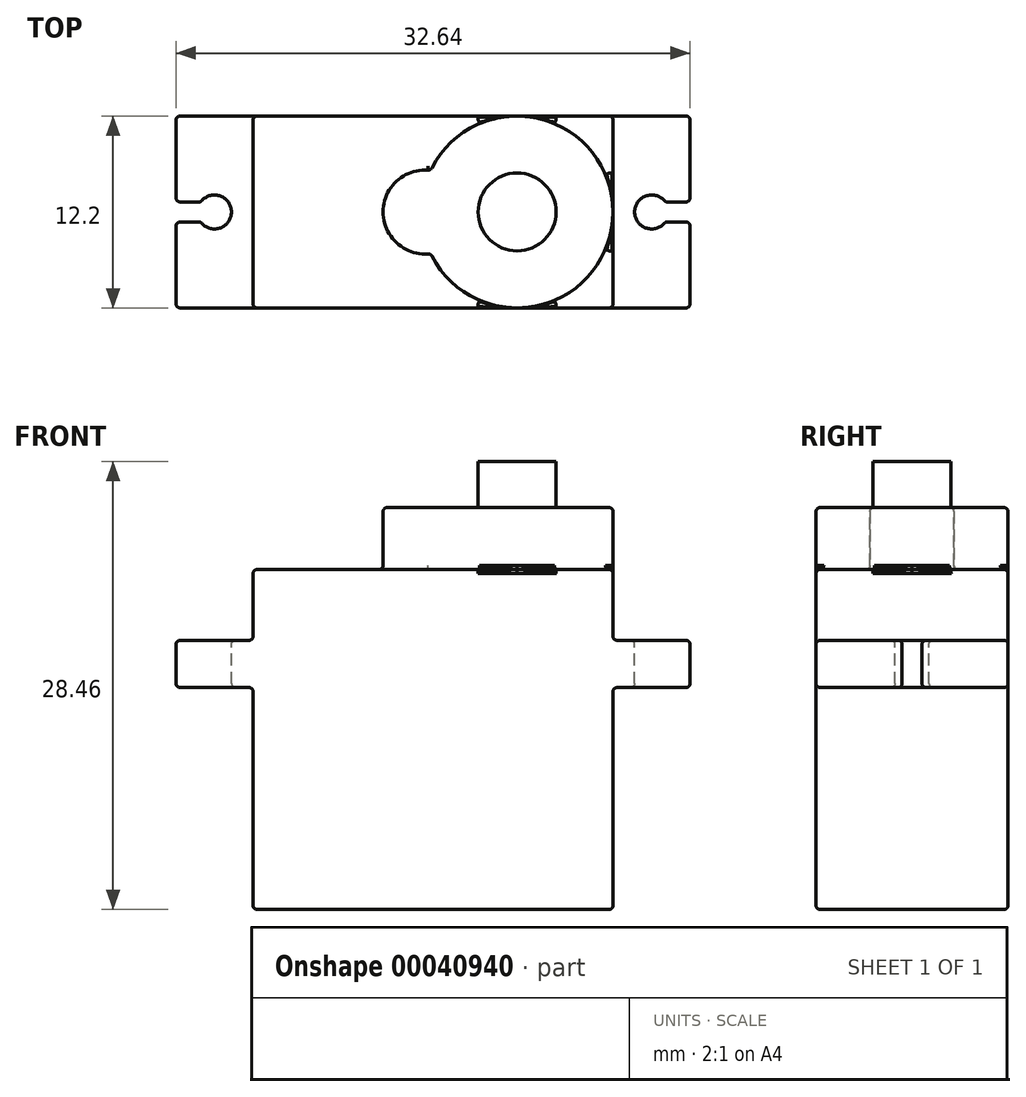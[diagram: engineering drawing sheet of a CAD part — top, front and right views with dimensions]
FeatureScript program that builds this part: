
annotation { "Feature Type Name" : "Feature", "Feature Type Description" : "" }
export const myFeature = defineFeature(function(context is Context, id is Id, definition is map)
    precondition{}
    {
        {
            var Q0;
            Q0=qCreatedBy(makeId("Top.planeOp"),FACE);
            var sketch = newSketch(context, id + "F0", { "sketchPlane" : qUnion([Q0])});
            skLineSegment(sketch, "E0.rect.bottom", {"start": v(11.43, 6.1) * mm, "end": v(-11.43, 6.1) * mm});
            skLineSegment(sketch, "E0.rect.top", {"start": v(11.43, -6.1) * mm, "end": v(-11.43, -6.1) * mm});
            skLineSegment(sketch, "E0.rect.left", {"start": v(11.43, 6.1) * mm, "end": v(11.43, -6.1) * mm});
            skLineSegment(sketch, "E0.rect.right", {"start": v(-11.43, 6.1) * mm, "end": v(-11.43, -6.1) * mm});
            skPoint(sketch, "E0.rect.middle", {"position": v(0, 0) * mm});
            skSolve(sketch);
        }
        {
            var Q0;
            Q0=makeQuery(id+"F0.imprint","IMPRINT",FACE,{"disambiguationData":[TD([[makeQuery(id+"F0.imprint","IMPRINT",EDGE,{"derivedFrom":sQuery(id+"F0.wireOp",EDGE,"E0.rect.bottom")}),1.0]])]});
            extrude(context, id + "F1", {"entities" : qUnion([Q0]), "depth" : 4.5 * mm});
        }
        {
            var Q0;
            Q0=qCreatedBy(makeId("Top.planeOp"),FACE);
            var sketch = newSketch(context, id + "F2", { "sketchPlane" : qUnion([Q0])});
            skLineSegment(sketch, "E1.rect.bottom", {"start": v(-16.32, 6.1) * mm, "end": v(16.32, 6.1) * mm});
            skLineSegment(sketch, "E1.rect.top", {"start": v(-16.32, -6.1) * mm, "end": v(16.32, -6.1) * mm});
            skLineSegment(sketch, "E1.rect.left", {"start": v(-16.32, 6.1) * mm, "end": v(-16.32, 0.64) * mm});
            skLineSegment(sketch, "E1.rect.right", {"start": v(16.32, 6.1) * mm, "end": v(16.32, 0.64) * mm});
            skPoint(sketch, "E1.rect.middle", {"position": v(0, 0) * mm});
            skArc(sketch, "E2", {"start": v(-14.75, -0.64) * mm, "mid": v(-12.8, 0) * mm, "end": v(-14.75, 0.64) * mm});
            skArc(sketch, "E3", {"start": v(14.75, 0.64) * mm, "mid": v(12.8, 0) * mm, "end": v(14.75, -0.64) * mm});
            skLineSegment(sketch, "E4.rect.bottom", {"start": v(-16.32, 0.64) * mm, "end": v(-14.75, 0.64) * mm});
            skLineSegment(sketch, "E4.rect.top", {"start": v(-16.32, -0.64) * mm, "end": v(-14.75, -0.64) * mm});
            skLineSegment(sketch, "E5.rect.bottom", {"start": v(16.32, 0.64) * mm, "end": v(14.75, 0.64) * mm});
            skLineSegment(sketch, "E5.rect.top", {"start": v(16.32, -0.64) * mm, "end": v(14.75, -0.64) * mm});
            skLineSegment(sketch, "E6.trimOffspring", {"start": v(16.32, -0.64) * mm, "end": v(16.32, -6.1) * mm});
            skLineSegment(sketch, "E7.trimOffspring", {"start": v(-16.32, -0.63) * mm, "end": v(-16.32, -6.1) * mm});
            skSolve(sketch);
        }
        {
            var Q0;
            Q0=makeQuery(id+"F2.imprint","IMPRINT",FACE,{"disambiguationData":[TD([[makeQuery(id+"F2.imprint","IMPRINT",EDGE,{"derivedFrom":sQuery(id+"F2.wireOp",EDGE,"E1.rect.bottom")}),-1.0]])]});
            extrude(context, id + "F3", {"entities" : qUnion([Q0]), "operationType" : NewBodyOperationType.ADD, "oppositeDirection" : true, "depth" : 3 * mm});
        }
        {
            var Q0;
            Q0=makeQuery(id+"F3.opExtrude","CAP_FACE",FACE,{"disambiguationData":[OSD([sQuery(id+"F2.wireOp",EDGE,"E1.rect.bottom"),sQuery(id+"F2.wireOp",EDGE,"E1.rect.top"),sQuery(id+"F2.wireOp",EDGE,"E1.rect.left"),sQuery(id+"F2.wireOp",EDGE,"E1.rect.right"),sQuery(id+"F2.wireOp",EDGE,"E2"),sQuery(id+"F2.wireOp",EDGE,"E3"),sQuery(id+"F2.wireOp",EDGE,"E4.rect.bottom"),sQuery(id+"F2.wireOp",EDGE,"E4.rect.top"),sQuery(id+"F2.wireOp",EDGE,"E5.rect.bottom"),sQuery(id+"F2.wireOp",EDGE,"E5.rect.top"),sQuery(id+"F2.wireOp",EDGE,"E6.trimOffspring"),sQuery(id+"F2.wireOp",EDGE,"E7.trimOffspring")])],"isStart":false});
            var sketch = newSketch(context, id + "F4", { "sketchPlane" : qUnion([Q0])});
            skLineSegment(sketch, "E8.rect.bottom", {"start": v(11.43, 6.1) * mm, "end": v(-11.43, 6.1) * mm});
            skLineSegment(sketch, "E8.rect.top", {"start": v(11.43, -6.1) * mm, "end": v(-11.43, -6.1) * mm});
            skLineSegment(sketch, "E8.rect.left", {"start": v(11.43, 6.1) * mm, "end": v(11.43, -6.1) * mm});
            skLineSegment(sketch, "E8.rect.right", {"start": v(-11.43, 6.1) * mm, "end": v(-11.43, -6.1) * mm});
            skPoint(sketch, "E8.rect.middle", {"position": v(0, 0) * mm});
            skSolve(sketch);
        }
        {
            var Q0;
            Q0=makeQuery(id+"F4.imprint","IMPRINT",FACE,{"disambiguationData":[TD([[makeQuery(id+"F4.imprint","IMPRINT",EDGE,{"derivedFrom":sQuery(id+"F4.wireOp",EDGE,"E8.rect.bottom")}),-1.0]])]});
            extrude(context, id + "F5", {"entities" : qUnion([Q0]), "operationType" : NewBodyOperationType.ADD, "depth" : 14.1 * mm});
        }
        {
            var Q0;
            Q0=makeQuery(id+"F1.opExtrude","CAP_FACE",FACE,{"disambiguationData":[OSD([sQuery(id+"F0.wireOp",EDGE,"E0.rect.bottom"),sQuery(id+"F0.wireOp",EDGE,"E0.rect.top"),sQuery(id+"F0.wireOp",EDGE,"E0.rect.left"),sQuery(id+"F0.wireOp",EDGE,"E0.rect.right")])],"isStart":false});
            var sketch = newSketch(context, id + "F6", { "sketchPlane" : qUnion([Q0])});
            skArc(sketch, "E9", {"start": v(-0.16, -2.64) * mm, "mid": v(11.43, 0) * mm, "end": v(-0.16, 2.64) * mm});
            skArc(sketch, "E10", {"start": v(-0.16, 2.64) * mm, "mid": v(-3.17, 0) * mm, "end": v(-0.16, -2.64) * mm});
            skLineSegment(sketch, "E11", {"start": v(-3.17, 0) * mm, "end": v(-3.17, -4.7) * mm});
            skSolve(sketch);
        }
        {
            var Q0;
            {var subQ0=sQuery(id+"F6.wireOp",EDGE,"E10");var subQ2=sQuery(id+"F6.wireOp",EDGE,"E9");var subQ3=makeQuery(id+"F6.imprint","INTERSECT",VERTEX,{"disambiguationData":[OD(0.0)],"derivedFrom":[subQ2,subQ0]});Q0=makeQuery(id+"F6.imprint","IMPRINT",FACE,{"disambiguationData":[TD([[makeQuery(id+"F6.imprint","IMPRINT",EDGE,{"disambiguationData":[TD([[subQ3,-1.0]])],"derivedFrom":subQ2}),1.0]])]});}
            extrude(context, id + "F7", {"entities" : qUnion([Q0]), "operationType" : NewBodyOperationType.ADD, "depth" : 3.94 * mm});
        }
        {
            var Q0;
            Q0=makeQuery(id+"F5.opExtrude","SWEPT_EDGE",EDGE,{"disambiguationData":[OSD([sQuery(id+"F2.wireOp",EDGE,"E1.rect.top"),sQuery(id+"F4.wireOp",EDGE,"E8.rect.bottom"),sQuery(id+"F4.wireOp",EDGE,"E8.rect.right")])]});
            var Q1;
            Q1=makeQuery(id+"F5.boolean.opBoolean","MERGE",FACE,{"derivedFrom":[makeQuery(id+"F3.boolean.opBoolean","MERGE",FACE,{"derivedFrom":[makeQuery(id+"F1.opExtrude","SWEPT_FACE",FACE,{"disambiguationData":[OSD([sQuery(id+"F0.wireOp",EDGE,"E0.rect.top")])]}),makeQuery(id+"F3.opExtrude","SWEPT_FACE",FACE,{"disambiguationData":[OSD([sQuery(id+"F2.wireOp",EDGE,"E1.rect.top")])]})]}),makeQuery(id+"F5.opExtrude","SWEPT_FACE",FACE,{"disambiguationData":[OSD([sQuery(id+"F4.wireOp",EDGE,"E8.rect.bottom")])]})]});
            var Q2;
            Q2=makeQuery(id+"F5.boolean.opBoolean","MERGE",FACE,{"derivedFrom":[makeQuery(id+"F3.boolean.opBoolean","MERGE",FACE,{"derivedFrom":[makeQuery(id+"F1.opExtrude","SWEPT_FACE",FACE,{"disambiguationData":[OSD([sQuery(id+"F0.wireOp",EDGE,"E0.rect.bottom")])]}),makeQuery(id+"F3.opExtrude","SWEPT_FACE",FACE,{"disambiguationData":[OSD([sQuery(id+"F2.wireOp",EDGE,"E1.rect.bottom")])]})]}),makeQuery(id+"F5.opExtrude","SWEPT_FACE",FACE,{"disambiguationData":[OSD([sQuery(id+"F4.wireOp",EDGE,"E8.rect.top")])]})]});
            var Q3;
            Q3=makeQuery(id+"F1.opExtrude","SWEPT_FACE",FACE,{"disambiguationData":[OSD([sQuery(id+"F0.wireOp",EDGE,"E0.rect.right")])]});
            var Q4;
            Q4=makeQuery(id+"F3.opExtrude","SWEPT_FACE",FACE,{"disambiguationData":[OSD([sQuery(id+"F2.wireOp",EDGE,"E1.rect.left")])]});
            var Q5;
            Q5=makeQuery(id+"F3.opExtrude","SWEPT_FACE",FACE,{"disambiguationData":[OSD([sQuery(id+"F2.wireOp",EDGE,"E7.trimOffspring")])]});
            var Q6;
            {var subQ0=sQuery(id+"F2.wireOp",EDGE,"E1.rect.bottom");var subQ1=sQuery(id+"F2.wireOp",EDGE,"E1.rect.top");var subQ2=sQuery(id+"F2.wireOp",EDGE,"E1.rect.left");var subQ3=sQuery(id+"F2.wireOp",EDGE,"E2");var subQ4=sQuery(id+"F2.wireOp",EDGE,"E4.rect.bottom");var subQ5=sQuery(id+"F2.wireOp",EDGE,"E4.rect.top");var subQ6=sQuery(id+"F2.wireOp",EDGE,"E7.trimOffspring");Q6=makeQuery(id+"F3.boolean.opBoolean","SPLIT",FACE,{"disambiguationData":[TD([makeQuery(id+"F1.opExtrude","SWEPT_FACE",FACE,{"disambiguationData":[OSD([sQuery(id+"F0.wireOp",EDGE,"E0.rect.right")])]})])],"derivedFrom":makeQuery(id+"F3.opExtrude","CAP_FACE",FACE,{"disambiguationData":[OSD([subQ0,subQ1,subQ2,sQuery(id+"F2.wireOp",EDGE,"E1.rect.right"),subQ3,sQuery(id+"F2.wireOp",EDGE,"E3"),subQ4,subQ5,sQuery(id+"F2.wireOp",EDGE,"E5.rect.bottom"),sQuery(id+"F2.wireOp",EDGE,"E5.rect.top"),sQuery(id+"F2.wireOp",EDGE,"E6.trimOffspring"),subQ6])],"isStart":true})});}
            var Q7;
            Q7=makeQuery(id+"F5.opExtrude","SWEPT_FACE",FACE,{"disambiguationData":[OSD([sQuery(id+"F4.wireOp",EDGE,"E8.rect.right")])]});
            var Q8;
            Q8=makeQuery(id+"F7.opExtrude","CAP_FACE",FACE,{"disambiguationData":[OSD([sQuery(id+"F6.wireOp",EDGE,"E9"),sQuery(id+"F6.wireOp",EDGE,"E10")])],"isStart":false});
            var Q9;
            {var subQ0=sQuery(id+"F0.wireOp",EDGE,"E0.rect.bottom");var subQ1=sQuery(id+"F0.wireOp",EDGE,"E0.rect.top");var subQ2=sQuery(id+"F0.wireOp",EDGE,"E0.rect.right");var subQ3=makeQuery(id+"F1.opExtrude","CAP_FACE",FACE,{"disambiguationData":[OSD([subQ0,subQ1,sQuery(id+"F0.wireOp",EDGE,"E0.rect.left"),subQ2])],"isStart":false});Q9=makeQuery(id+"F7.boolean.opBoolean","SPLIT",FACE,{"disambiguationData":[TD([makeQuery(id+"F1.opExtrude","SWEPT_FACE",FACE,{"disambiguationData":[OSD([subQ0])]}),subQ3,makeQuery(id+"F1.opExtrude","SWEPT_FACE",FACE,{"disambiguationData":[OSD([subQ1])]}),makeQuery(id+"F1.opExtrude","SWEPT_FACE",FACE,{"disambiguationData":[OSD([subQ2])]}),makeQuery(id+"F3.opExtrude","SWEPT_FACE",FACE,{"disambiguationData":[OSD([sQuery(id+"F2.wireOp",EDGE,"E1.rect.bottom")])]}),makeQuery(id+"F3.opExtrude","SWEPT_FACE",FACE,{"disambiguationData":[OSD([sQuery(id+"F2.wireOp",EDGE,"E1.rect.top")])]}),makeQuery(id+"F5.opExtrude","SWEPT_FACE",FACE,{"disambiguationData":[OSD([sQuery(id+"F4.wireOp",EDGE,"E8.rect.bottom")])]}),makeQuery(id+"F5.opExtrude","SWEPT_FACE",FACE,{"disambiguationData":[OSD([sQuery(id+"F4.wireOp",EDGE,"E8.rect.top")])]}),makeQuery(id+"F7.opExtrude","SWEPT_FACE",FACE,{"disambiguationData":[OSD([sQuery(id+"F6.wireOp",EDGE,"E9")])]}),makeQuery(id+"F7.opExtrude","SWEPT_FACE",FACE,{"disambiguationData":[OSD([sQuery(id+"F6.wireOp",EDGE,"E10")])]})])],"derivedFrom":subQ3});}
            var Q10;
            Q10=makeQuery(id+"F3.opExtrude","CAP_EDGE",EDGE,{"disambiguationData":[OSD([sQuery(id+"F2.wireOp",EDGE,"E3")])],"isStart":false});
            var Q11;
            Q11=makeQuery(id+"F5.opExtrude","SWEPT_FACE",FACE,{"disambiguationData":[OSD([sQuery(id+"F4.wireOp",EDGE,"E8.rect.left")])]});
            var Q12;
            Q12=makeQuery(id+"F1.opExtrude","SWEPT_FACE",FACE,{"disambiguationData":[OSD([sQuery(id+"F0.wireOp",EDGE,"E0.rect.left")])]});
            var Q13;
            {var subQ0=sQuery(id+"F2.wireOp",EDGE,"E1.rect.bottom");var subQ1=sQuery(id+"F2.wireOp",EDGE,"E1.rect.top");var subQ2=sQuery(id+"F2.wireOp",EDGE,"E1.rect.right");var subQ3=sQuery(id+"F2.wireOp",EDGE,"E3");var subQ4=sQuery(id+"F2.wireOp",EDGE,"E5.rect.bottom");var subQ5=sQuery(id+"F2.wireOp",EDGE,"E5.rect.top");var subQ6=sQuery(id+"F2.wireOp",EDGE,"E6.trimOffspring");Q13=makeQuery(id+"F3.boolean.opBoolean","SPLIT",FACE,{"disambiguationData":[TD([makeQuery(id+"F1.opExtrude","SWEPT_FACE",FACE,{"disambiguationData":[OSD([sQuery(id+"F0.wireOp",EDGE,"E0.rect.left")])]})])],"derivedFrom":makeQuery(id+"F3.opExtrude","CAP_FACE",FACE,{"disambiguationData":[OSD([subQ0,subQ1,sQuery(id+"F2.wireOp",EDGE,"E1.rect.left"),subQ2,sQuery(id+"F2.wireOp",EDGE,"E2"),subQ3,sQuery(id+"F2.wireOp",EDGE,"E4.rect.bottom"),sQuery(id+"F2.wireOp",EDGE,"E4.rect.top"),subQ4,subQ5,subQ6,sQuery(id+"F2.wireOp",EDGE,"E7.trimOffspring")])],"isStart":true})});}
            var Q14;
            Q14=makeQuery(id+"F5.opExtrude","SWEPT_EDGE",EDGE,{"disambiguationData":[OSD([sQuery(id+"F2.wireOp",EDGE,"E1.rect.top"),sQuery(id+"F4.wireOp",EDGE,"E8.rect.bottom"),sQuery(id+"F4.wireOp",EDGE,"E8.rect.left")])]});
            var Q15;
            Q15=makeQuery(id+"F5.opExtrude","SWEPT_EDGE",EDGE,{"disambiguationData":[OSD([sQuery(id+"F2.wireOp",EDGE,"E1.rect.bottom"),sQuery(id+"F4.wireOp",EDGE,"E8.rect.top"),sQuery(id+"F4.wireOp",EDGE,"E8.rect.left")])]});
            var Q16;
            Q16=makeQuery(id+"F3.opExtrude","CAP_EDGE",EDGE,{"disambiguationData":[OSD([sQuery(id+"F2.wireOp",EDGE,"E6.trimOffspring")])],"isStart":true});
            var Q17;
            Q17=makeQuery(id+"F3.opExtrude","CAP_EDGE",EDGE,{"disambiguationData":[OSD([sQuery(id+"F2.wireOp",EDGE,"E1.rect.left")])],"isStart":true});
            var Q18;
            Q18=makeQuery(id+"F5.opExtrude","CAP_EDGE",EDGE,{"disambiguationData":[OSD([sQuery(id+"F4.wireOp",EDGE,"E8.rect.bottom")])],"isStart":false});
            var Q19;
            {var subQ0=sQuery(id+"F2.wireOp",EDGE,"E1.rect.bottom");var subQ1=sQuery(id+"F2.wireOp",EDGE,"E1.rect.right");Q19=makeQuery(id+"F5.boolean.opBoolean","SPLIT",EDGE,{"disambiguationData":[TD([makeQuery(id+"F3.opExtrude","SWEPT_FACE",FACE,{"disambiguationData":[OSD([subQ1])]})])],"derivedFrom":makeQuery(id+"F3.opExtrude","CAP_EDGE",EDGE,{"disambiguationData":[OSD([subQ0])],"isStart":false})});}
            var Q20;
            Q20=makeQuery(id+"F5.opExtrude","CAP_EDGE",EDGE,{"disambiguationData":[OSD([sQuery(id+"F4.wireOp",EDGE,"E8.rect.left")])],"isStart":false});
            var Q21;
            {var subQ0=sQuery(id+"F2.wireOp",EDGE,"E1.rect.top");var subQ1=sQuery(id+"F2.wireOp",EDGE,"E6.trimOffspring");Q21=makeQuery(id+"F5.boolean.opBoolean","SPLIT",EDGE,{"disambiguationData":[TD([makeQuery(id+"F3.opExtrude","SWEPT_FACE",FACE,{"disambiguationData":[OSD([subQ1])]})])],"derivedFrom":makeQuery(id+"F3.opExtrude","CAP_EDGE",EDGE,{"disambiguationData":[OSD([subQ0])],"isStart":false})});}
            var Q22;
            Q22=makeQuery(id+"F3.opExtrude","SWEPT_EDGE",EDGE,{"disambiguationData":[OSD([sQuery(id+"F2.wireOp",EDGE,"E5.rect.top"),sQuery(id+"F2.wireOp",EDGE,"E6.trimOffspring")])]});
            var Q23;
            {var subQ0=sQuery(id+"F2.wireOp",EDGE,"E1.rect.top");Q23=makeQuery(id+"F3.boolean.opBoolean","SPLIT",EDGE,{"disambiguationData":[TD([makeQuery(id+"F1.opExtrude","SWEPT_FACE",FACE,{"disambiguationData":[OSD([sQuery(id+"F0.wireOp",EDGE,"E0.rect.right")])]})])],"derivedFrom":makeQuery(id+"F3.opExtrude","CAP_EDGE",EDGE,{"disambiguationData":[OSD([subQ0])],"isStart":true})});}
            var Q24;
            {var subQ0=sQuery(id+"F2.wireOp",EDGE,"E1.rect.top");Q24=makeQuery(id+"F3.boolean.opBoolean","SPLIT",EDGE,{"disambiguationData":[TD([makeQuery(id+"F1.opExtrude","SWEPT_FACE",FACE,{"disambiguationData":[OSD([sQuery(id+"F0.wireOp",EDGE,"E0.rect.left")])]})])],"derivedFrom":makeQuery(id+"F3.opExtrude","CAP_EDGE",EDGE,{"disambiguationData":[OSD([subQ0])],"isStart":true})});}
            var Q25;
            Q25=makeQuery(id+"F3.opExtrude","SWEPT_EDGE",EDGE,{"disambiguationData":[OSD([sQuery(id+"F2.wireOp",EDGE,"E3"),sQuery(id+"F2.wireOp",EDGE,"E5.rect.top")])]});
            var Q26;
            {var subQ0=sQuery(id+"F2.wireOp",EDGE,"E1.rect.bottom");Q26=makeQuery(id+"F3.boolean.opBoolean","SPLIT",EDGE,{"disambiguationData":[TD([makeQuery(id+"F1.opExtrude","SWEPT_FACE",FACE,{"disambiguationData":[OSD([sQuery(id+"F0.wireOp",EDGE,"E0.rect.left")])]})])],"derivedFrom":makeQuery(id+"F3.opExtrude","CAP_EDGE",EDGE,{"disambiguationData":[OSD([subQ0])],"isStart":true})});}
            var Q27;
            Q27=makeQuery(id+"F1.opExtrude","CAP_EDGE",EDGE,{"disambiguationData":[OSD([sQuery(id+"F0.wireOp",EDGE,"E0.rect.left")])],"isStart":true});
            var Q28;
            Q28=makeQuery(id+"F3.opExtrude","SWEPT_EDGE",EDGE,{"disambiguationData":[OSD([sQuery(id+"F2.wireOp",EDGE,"E3"),sQuery(id+"F2.wireOp",EDGE,"E5.rect.bottom")])]});
            var Q29;
            Q29=makeQuery(id+"F3.opExtrude","CAP_EDGE",EDGE,{"disambiguationData":[OSD([sQuery(id+"F2.wireOp",EDGE,"E5.rect.bottom")])],"isStart":true});
            var Q30;
            Q30=makeQuery(id+"F3.opExtrude","CAP_EDGE",EDGE,{"disambiguationData":[OSD([sQuery(id+"F2.wireOp",EDGE,"E1.rect.right")])],"isStart":false});
            var Q31;
            Q31=makeQuery(id+"F3.opExtrude","SWEPT_EDGE",EDGE,{"disambiguationData":[OSD([sQuery(id+"F2.wireOp",EDGE,"E1.rect.right"),sQuery(id+"F2.wireOp",EDGE,"E5.rect.bottom")])]});
            var Q32;
            Q32=makeQuery(id+"F3.opExtrude","SWEPT_EDGE",EDGE,{"disambiguationData":[OSD([sQuery(id+"F2.wireOp",EDGE,"E1.rect.top"),sQuery(id+"F2.wireOp",EDGE,"E7.trimOffspring")])]});
            var Q33;
            Q33=makeQuery(id+"F3.opExtrude","SWEPT_EDGE",EDGE,{"disambiguationData":[OSD([sQuery(id+"F2.wireOp",EDGE,"E1.rect.bottom"),sQuery(id+"F2.wireOp",EDGE,"E1.rect.right")])]});
            var Q34;
            Q34=makeQuery(id+"F1.opExtrude","SWEPT_EDGE",EDGE,{"disambiguationData":[OSD([sQuery(id+"F0.wireOp",EDGE,"E0.rect.bottom"),sQuery(id+"F0.wireOp",EDGE,"E0.rect.left")])]});
            var Q35;
            Q35=makeQuery(id+"F1.opExtrude","SWEPT_EDGE",EDGE,{"disambiguationData":[OSD([sQuery(id+"F0.wireOp",EDGE,"E0.rect.bottom"),sQuery(id+"F0.wireOp",EDGE,"E0.rect.right")])]});
            var Q36;
            Q36=makeQuery(id+"F1.opExtrude","SWEPT_EDGE",EDGE,{"disambiguationData":[OSD([sQuery(id+"F0.wireOp",EDGE,"E0.rect.top"),sQuery(id+"F0.wireOp",EDGE,"E0.rect.left")])]});
            var Q37;
            Q37=makeQuery(id+"F1.opExtrude","SWEPT_EDGE",EDGE,{"disambiguationData":[OSD([sQuery(id+"F0.wireOp",EDGE,"E0.rect.top"),sQuery(id+"F0.wireOp",EDGE,"E0.rect.right")])]});
            var Q38;
            Q38=makeQuery(id+"F3.opExtrude","CAP_EDGE",EDGE,{"disambiguationData":[OSD([sQuery(id+"F2.wireOp",EDGE,"E3")])],"isStart":true});
            var Q39;
            Q39=makeQuery(id+"F1.opExtrude","CAP_EDGE",EDGE,{"disambiguationData":[OSD([sQuery(id+"F0.wireOp",EDGE,"E0.rect.right")])],"isStart":false});
            var Q40;
            {var subQ0=sQuery(id+"F2.wireOp",EDGE,"E1.rect.top");var subQ1=sQuery(id+"F2.wireOp",EDGE,"E7.trimOffspring");Q40=makeQuery(id+"F5.boolean.opBoolean","SPLIT",EDGE,{"disambiguationData":[TD([makeQuery(id+"F3.opExtrude","SWEPT_FACE",FACE,{"disambiguationData":[OSD([subQ1])]})])],"derivedFrom":makeQuery(id+"F3.opExtrude","CAP_EDGE",EDGE,{"disambiguationData":[OSD([subQ0])],"isStart":false})});}
            var Q41;
            Q41=makeQuery(id+"F3.opExtrude","CAP_EDGE",EDGE,{"disambiguationData":[OSD([sQuery(id+"F2.wireOp",EDGE,"E6.trimOffspring")])],"isStart":false});
            var Q42;
            {var subQ0=sQuery(id+"F6.wireOp",EDGE,"E9");var subQ1=sQuery(id+"F0.wireOp",EDGE,"E0.rect.left");var subQ2=sQuery(id+"F0.wireOp",EDGE,"E0.rect.top");Q42=makeQuery(id+"F7.boolean.opBoolean","SPLIT",EDGE,{"disambiguationData":[TD([makeQuery(id+"F1.opExtrude","CAP_FACE",FACE,{"disambiguationData":[OSD([sQuery(id+"F0.wireOp",EDGE,"E0.rect.bottom"),subQ2,subQ1,sQuery(id+"F0.wireOp",EDGE,"E0.rect.right")])],"isStart":false}),makeQuery(id+"F1.opExtrude","SWEPT_FACE",FACE,{"disambiguationData":[OSD([subQ2])]}),makeQuery(id+"F1.opExtrude","SWEPT_FACE",FACE,{"disambiguationData":[OSD([subQ1])]}),makeQuery(id+"F3.opExtrude","SWEPT_FACE",FACE,{"disambiguationData":[OSD([sQuery(id+"F2.wireOp",EDGE,"E1.rect.top")])]}),makeQuery(id+"F5.opExtrude","SWEPT_FACE",FACE,{"disambiguationData":[OSD([sQuery(id+"F4.wireOp",EDGE,"E8.rect.bottom")])]}),makeQuery(id+"F7.opExtrude","SWEPT_FACE",FACE,{"disambiguationData":[OSD([subQ0])]})])],"derivedFrom":makeQuery(id+"F7.opExtrude","CAP_EDGE",EDGE,{"disambiguationData":[OSD([subQ0])],"isStart":true})});}
            var Q43;
            Q43=makeQuery(id+"F7.opExtrude","CAP_EDGE",EDGE,{"disambiguationData":[OSD([sQuery(id+"F6.wireOp",EDGE,"E9")])],"isStart":false});
            var Q44;
            {var subQ0=sQuery(id+"F6.wireOp",EDGE,"E9");var subQ1=sQuery(id+"F0.wireOp",EDGE,"E0.rect.left");var subQ2=sQuery(id+"F0.wireOp",EDGE,"E0.rect.bottom");Q44=makeQuery(id+"F7.boolean.opBoolean","SPLIT",EDGE,{"disambiguationData":[TD([makeQuery(id+"F1.opExtrude","SWEPT_FACE",FACE,{"disambiguationData":[OSD([subQ2])]}),makeQuery(id+"F1.opExtrude","CAP_FACE",FACE,{"disambiguationData":[OSD([subQ2,sQuery(id+"F0.wireOp",EDGE,"E0.rect.top"),subQ1,sQuery(id+"F0.wireOp",EDGE,"E0.rect.right")])],"isStart":false}),makeQuery(id+"F1.opExtrude","SWEPT_FACE",FACE,{"disambiguationData":[OSD([subQ1])]}),makeQuery(id+"F3.opExtrude","SWEPT_FACE",FACE,{"disambiguationData":[OSD([sQuery(id+"F2.wireOp",EDGE,"E1.rect.bottom")])]}),makeQuery(id+"F5.opExtrude","SWEPT_FACE",FACE,{"disambiguationData":[OSD([sQuery(id+"F4.wireOp",EDGE,"E8.rect.top")])]}),makeQuery(id+"F7.opExtrude","SWEPT_FACE",FACE,{"disambiguationData":[OSD([subQ0])]})])],"derivedFrom":makeQuery(id+"F7.opExtrude","CAP_EDGE",EDGE,{"disambiguationData":[OSD([subQ0])],"isStart":true})});}
            var Q45;
            Q45=makeQuery(id+"F7.opExtrude","CAP_EDGE",EDGE,{"disambiguationData":[OSD([sQuery(id+"F6.wireOp",EDGE,"E10")])],"isStart":false});
            var Q46;
            Q46=makeQuery(id+"F5.opExtrude","SWEPT_EDGE",EDGE,{"disambiguationData":[OSD([sQuery(id+"F2.wireOp",EDGE,"E1.rect.bottom"),sQuery(id+"F4.wireOp",EDGE,"E8.rect.top"),sQuery(id+"F4.wireOp",EDGE,"E8.rect.right")])]});
            var Q47;
            Q47=makeQuery(id+"F5.opExtrude","CAP_EDGE",EDGE,{"disambiguationData":[OSD([sQuery(id+"F4.wireOp",EDGE,"E8.rect.top")])],"isStart":false});
            var Q48;
            Q48=makeQuery(id+"F5.opExtrude","CAP_EDGE",EDGE,{"disambiguationData":[OSD([sQuery(id+"F4.wireOp",EDGE,"E8.rect.left")])],"isStart":true});
            var Q49;
            Q49=makeQuery(id+"F3.opExtrude","CAP_EDGE",EDGE,{"disambiguationData":[OSD([sQuery(id+"F2.wireOp",EDGE,"E2")])],"isStart":true});
            var Q50;
            Q50=makeQuery(id+"F5.opExtrude","CAP_EDGE",EDGE,{"disambiguationData":[OSD([sQuery(id+"F4.wireOp",EDGE,"E8.rect.right")])],"isStart":false});
            var Q51;
            {var subQ0=sQuery(id+"F2.wireOp",EDGE,"E1.rect.bottom");var subQ1=sQuery(id+"F2.wireOp",EDGE,"E1.rect.left");Q51=makeQuery(id+"F5.boolean.opBoolean","SPLIT",EDGE,{"disambiguationData":[TD([makeQuery(id+"F3.opExtrude","SWEPT_FACE",FACE,{"disambiguationData":[OSD([subQ1])]})])],"derivedFrom":makeQuery(id+"F3.opExtrude","CAP_EDGE",EDGE,{"disambiguationData":[OSD([subQ0])],"isStart":false})});}
            var Q52;
            Q52=makeQuery(id+"F5.opExtrude","CAP_EDGE",EDGE,{"disambiguationData":[OSD([sQuery(id+"F4.wireOp",EDGE,"E8.rect.right")])],"isStart":true});
            var Q53;
            Q53=makeQuery(id+"F3.opExtrude","CAP_EDGE",EDGE,{"disambiguationData":[OSD([sQuery(id+"F2.wireOp",EDGE,"E5.rect.bottom")])],"isStart":false});
            var Q54;
            {var subQ0=sQuery(id+"F2.wireOp",EDGE,"E1.rect.bottom");Q54=makeQuery(id+"F3.boolean.opBoolean","SPLIT",EDGE,{"disambiguationData":[TD([makeQuery(id+"F1.opExtrude","SWEPT_FACE",FACE,{"disambiguationData":[OSD([sQuery(id+"F0.wireOp",EDGE,"E0.rect.right")])]})])],"derivedFrom":makeQuery(id+"F3.opExtrude","CAP_EDGE",EDGE,{"disambiguationData":[OSD([subQ0])],"isStart":true})});}
            var Q55;
            Q55=makeQuery(id+"F3.opExtrude","SWEPT_EDGE",EDGE,{"disambiguationData":[OSD([sQuery(id+"F2.wireOp",EDGE,"E4.rect.top"),sQuery(id+"F2.wireOp",EDGE,"E7.trimOffspring")])]});
            var Q56;
            Q56=makeQuery(id+"F1.opExtrude","CAP_EDGE",EDGE,{"disambiguationData":[OSD([sQuery(id+"F0.wireOp",EDGE,"E0.rect.right")])],"isStart":true});
            var Q57;
            Q57=makeQuery(id+"F3.opExtrude","CAP_EDGE",EDGE,{"disambiguationData":[OSD([sQuery(id+"F2.wireOp",EDGE,"E7.trimOffspring")])],"isStart":false});
            var Q58;
            Q58=makeQuery(id+"F3.opExtrude","SWEPT_EDGE",EDGE,{"disambiguationData":[OSD([sQuery(id+"F2.wireOp",EDGE,"E2"),sQuery(id+"F2.wireOp",EDGE,"E4.rect.top")])]});
            var Q59;
            Q59=makeQuery(id+"F3.opExtrude","SWEPT_EDGE",EDGE,{"disambiguationData":[OSD([sQuery(id+"F2.wireOp",EDGE,"E1.rect.left"),sQuery(id+"F2.wireOp",EDGE,"E4.rect.bottom")])]});
            var Q60;
            Q60=makeQuery(id+"F3.opExtrude","SWEPT_EDGE",EDGE,{"disambiguationData":[OSD([sQuery(id+"F2.wireOp",EDGE,"E1.rect.top"),sQuery(id+"F2.wireOp",EDGE,"E6.trimOffspring")])]});
            var Q61;
            Q61=makeQuery(id+"F3.opExtrude","SWEPT_EDGE",EDGE,{"disambiguationData":[OSD([sQuery(id+"F2.wireOp",EDGE,"E1.rect.bottom"),sQuery(id+"F2.wireOp",EDGE,"E1.rect.left")])]});
            var Q62;
            {var subQ0=sQuery(id+"F6.wireOp",EDGE,"E9");var subQ1=sQuery(id+"F6.wireOp",EDGE,"E10");Q62=makeQuery(id+"F7.opExtrude","SWEPT_EDGE",EDGE,{"disambiguationData":[OSD([subQ0,subQ1]),TDD([makeQuery(id+"F6.imprint","INTERSECT",VERTEX,{"disambiguationData":[OD(0.0)],"derivedFrom":[subQ0,subQ1]})])]});}
            var Q63;
            {var subQ0=sQuery(id+"F6.wireOp",EDGE,"E9");var subQ1=sQuery(id+"F0.wireOp",EDGE,"E0.rect.bottom");Q63=makeQuery(id+"F7.boolean.opBoolean","SPLIT",EDGE,{"disambiguationData":[TD([makeQuery(id+"F1.opExtrude","SWEPT_FACE",FACE,{"disambiguationData":[OSD([subQ1])]}),makeQuery(id+"F1.opExtrude","CAP_FACE",FACE,{"disambiguationData":[OSD([subQ1,sQuery(id+"F0.wireOp",EDGE,"E0.rect.top"),sQuery(id+"F0.wireOp",EDGE,"E0.rect.left"),sQuery(id+"F0.wireOp",EDGE,"E0.rect.right")])],"isStart":false}),makeQuery(id+"F3.opExtrude","SWEPT_FACE",FACE,{"disambiguationData":[OSD([sQuery(id+"F2.wireOp",EDGE,"E1.rect.bottom")])]}),makeQuery(id+"F5.opExtrude","SWEPT_FACE",FACE,{"disambiguationData":[OSD([sQuery(id+"F4.wireOp",EDGE,"E8.rect.top")])]}),makeQuery(id+"F7.opExtrude","SWEPT_FACE",FACE,{"disambiguationData":[OSD([subQ0])]}),makeQuery(id+"F7.opExtrude","SWEPT_FACE",FACE,{"disambiguationData":[OSD([sQuery(id+"F6.wireOp",EDGE,"E10")])]})])],"derivedFrom":makeQuery(id+"F7.opExtrude","CAP_EDGE",EDGE,{"disambiguationData":[OSD([subQ0])],"isStart":true})});}
            var Q64;
            {var subQ0=sQuery(id+"F0.wireOp",EDGE,"E0.rect.left");var subQ1=sQuery(id+"F0.wireOp",EDGE,"E0.rect.top");Q64=makeQuery(id+"F7.boolean.opBoolean","SPLIT",EDGE,{"disambiguationData":[TD([makeQuery(id+"F1.opExtrude","SWEPT_FACE",FACE,{"disambiguationData":[OSD([subQ1])]})])],"derivedFrom":makeQuery(id+"F1.opExtrude","CAP_EDGE",EDGE,{"disambiguationData":[OSD([subQ0])],"isStart":false})});}
            var Q65;
            Q65=makeQuery(id+"F3.opExtrude","CAP_EDGE",EDGE,{"disambiguationData":[OSD([sQuery(id+"F2.wireOp",EDGE,"E4.rect.bottom")])],"isStart":false});
            var Q66;
            Q66=makeQuery(id+"F3.opExtrude","CAP_EDGE",EDGE,{"disambiguationData":[OSD([sQuery(id+"F2.wireOp",EDGE,"E1.rect.right")])],"isStart":true});
            var Q67;
            Q67=makeQuery(id+"F3.opExtrude","CAP_EDGE",EDGE,{"disambiguationData":[OSD([sQuery(id+"F2.wireOp",EDGE,"E7.trimOffspring")])],"isStart":true});
            var Q68;
            Q68=makeQuery(id+"F3.opExtrude","CAP_EDGE",EDGE,{"disambiguationData":[OSD([sQuery(id+"F2.wireOp",EDGE,"E5.rect.top")])],"isStart":false});
            var Q69;
            Q69=makeQuery(id+"F3.opExtrude","CAP_EDGE",EDGE,{"disambiguationData":[OSD([sQuery(id+"F2.wireOp",EDGE,"E2")])],"isStart":false});
            var Q70;
            Q70=makeQuery(id+"F3.opExtrude","CAP_EDGE",EDGE,{"disambiguationData":[OSD([sQuery(id+"F2.wireOp",EDGE,"E1.rect.left")])],"isStart":false});
            var Q71;
            Q71=makeQuery(id+"F3.opExtrude","CAP_EDGE",EDGE,{"disambiguationData":[OSD([sQuery(id+"F2.wireOp",EDGE,"E5.rect.top")])],"isStart":true});
            var Q72;
            {var subQ0=sQuery(id+"F6.wireOp",EDGE,"E9");var subQ1=sQuery(id+"F0.wireOp",EDGE,"E0.rect.top");Q72=makeQuery(id+"F7.boolean.opBoolean","SPLIT",EDGE,{"disambiguationData":[TD([makeQuery(id+"F1.opExtrude","CAP_FACE",FACE,{"disambiguationData":[OSD([sQuery(id+"F0.wireOp",EDGE,"E0.rect.bottom"),subQ1,sQuery(id+"F0.wireOp",EDGE,"E0.rect.left"),sQuery(id+"F0.wireOp",EDGE,"E0.rect.right")])],"isStart":false}),makeQuery(id+"F1.opExtrude","SWEPT_FACE",FACE,{"disambiguationData":[OSD([subQ1])]}),makeQuery(id+"F3.opExtrude","SWEPT_FACE",FACE,{"disambiguationData":[OSD([sQuery(id+"F2.wireOp",EDGE,"E1.rect.top")])]}),makeQuery(id+"F5.opExtrude","SWEPT_FACE",FACE,{"disambiguationData":[OSD([sQuery(id+"F4.wireOp",EDGE,"E8.rect.bottom")])]}),makeQuery(id+"F7.opExtrude","SWEPT_FACE",FACE,{"disambiguationData":[OSD([subQ0])]}),makeQuery(id+"F7.opExtrude","SWEPT_FACE",FACE,{"disambiguationData":[OSD([sQuery(id+"F6.wireOp",EDGE,"E10")])]})])],"derivedFrom":makeQuery(id+"F7.opExtrude","CAP_EDGE",EDGE,{"disambiguationData":[OSD([subQ0])],"isStart":true})});}
            var Q73;
            {var subQ0=sQuery(id+"F6.wireOp",EDGE,"E9");var subQ1=sQuery(id+"F6.wireOp",EDGE,"E10");Q73=makeQuery(id+"F7.opExtrude","SWEPT_EDGE",EDGE,{"disambiguationData":[OSD([subQ0,subQ1]),TDD([makeQuery(id+"F6.imprint","INTERSECT",VERTEX,{"disambiguationData":[OD(1.0)],"derivedFrom":[subQ0,subQ1]})])]});}
            var Q74;
            {var subQ0=sQuery(id+"F0.wireOp",EDGE,"E0.rect.top");var subQ1=sQuery(id+"F0.wireOp",EDGE,"E0.rect.left");Q74=makeQuery(id+"F7.boolean.opBoolean","SPLIT",EDGE,{"disambiguationData":[TD([makeQuery(id+"F1.opExtrude","SWEPT_FACE",FACE,{"disambiguationData":[OSD([subQ1])]})])],"derivedFrom":makeQuery(id+"F1.opExtrude","CAP_EDGE",EDGE,{"disambiguationData":[OSD([subQ0])],"isStart":false})});}
            var Q75;
            {var subQ0=sQuery(id+"F0.wireOp",EDGE,"E0.rect.bottom");var subQ1=sQuery(id+"F0.wireOp",EDGE,"E0.rect.right");Q75=makeQuery(id+"F7.boolean.opBoolean","SPLIT",EDGE,{"disambiguationData":[TD([makeQuery(id+"F1.opExtrude","SWEPT_FACE",FACE,{"disambiguationData":[OSD([subQ1])]})])],"derivedFrom":makeQuery(id+"F1.opExtrude","CAP_EDGE",EDGE,{"disambiguationData":[OSD([subQ0])],"isStart":false})});}
            var Q76;
            {var subQ0=sQuery(id+"F0.wireOp",EDGE,"E0.rect.left");var subQ1=sQuery(id+"F0.wireOp",EDGE,"E0.rect.bottom");Q76=makeQuery(id+"F7.boolean.opBoolean","SPLIT",EDGE,{"disambiguationData":[TD([makeQuery(id+"F1.opExtrude","SWEPT_FACE",FACE,{"disambiguationData":[OSD([subQ1])]})])],"derivedFrom":makeQuery(id+"F1.opExtrude","CAP_EDGE",EDGE,{"disambiguationData":[OSD([subQ0])],"isStart":false})});}
            var Q77;
            {var subQ0=sQuery(id+"F0.wireOp",EDGE,"E0.rect.top");var subQ1=sQuery(id+"F0.wireOp",EDGE,"E0.rect.right");Q77=makeQuery(id+"F7.boolean.opBoolean","SPLIT",EDGE,{"disambiguationData":[TD([makeQuery(id+"F1.opExtrude","SWEPT_FACE",FACE,{"disambiguationData":[OSD([subQ1])]})])],"derivedFrom":makeQuery(id+"F1.opExtrude","CAP_EDGE",EDGE,{"disambiguationData":[OSD([subQ0])],"isStart":false})});}
            var Q78;
            Q78=makeQuery(id+"F7.opExtrude","CAP_EDGE",EDGE,{"disambiguationData":[OSD([sQuery(id+"F6.wireOp",EDGE,"E10")])],"isStart":true});
            var Q79;
            {var subQ0=sQuery(id+"F0.wireOp",EDGE,"E0.rect.bottom");var subQ1=sQuery(id+"F0.wireOp",EDGE,"E0.rect.left");Q79=makeQuery(id+"F7.boolean.opBoolean","SPLIT",EDGE,{"disambiguationData":[TD([makeQuery(id+"F1.opExtrude","SWEPT_FACE",FACE,{"disambiguationData":[OSD([subQ1])]})])],"derivedFrom":makeQuery(id+"F1.opExtrude","CAP_EDGE",EDGE,{"disambiguationData":[OSD([subQ0])],"isStart":false})});}
            var Q80;
            Q80=makeQuery(id+"F3.opExtrude","CAP_EDGE",EDGE,{"disambiguationData":[OSD([sQuery(id+"F2.wireOp",EDGE,"E4.rect.top")])],"isStart":false});
            var Q81;
            Q81=makeQuery(id+"F3.opExtrude","SWEPT_EDGE",EDGE,{"disambiguationData":[OSD([sQuery(id+"F2.wireOp",EDGE,"E2"),sQuery(id+"F2.wireOp",EDGE,"E4.rect.bottom")])]});
            var Q82;
            Q82=makeQuery(id+"F3.opExtrude","CAP_EDGE",EDGE,{"disambiguationData":[OSD([sQuery(id+"F2.wireOp",EDGE,"E4.rect.top")])],"isStart":true});
            var Q83;
            Q83=makeQuery(id+"F3.opExtrude","CAP_EDGE",EDGE,{"disambiguationData":[OSD([sQuery(id+"F2.wireOp",EDGE,"E4.rect.bottom")])],"isStart":true});
            fillet(context, id + "F8", {"entities" : qUnion([Q0, Q1, Q2, Q3, Q4, Q5, Q6, Q7, Q8, Q9, Q10, Q11, Q12, Q13, Q14, Q15, Q16, Q17, Q18, Q19, Q20, Q21, Q22, Q23, Q24, Q25, Q26, Q27, Q28, Q29, Q30, Q31, Q32, Q33, Q34, Q35, Q36, Q37, Q38, Q39, Q40, Q41, Q42, Q43, Q44, Q45, Q46, Q47, Q48, Q49, Q50, Q51, Q52, Q53, Q54, Q55, Q56, Q57, Q58, Q59, Q60, Q61, Q62, Q63, Q64, Q65, Q66, Q67, Q68, Q69, Q70, Q71, Q72, Q73, Q74, Q75, Q76, Q77, Q78, Q79, Q80, Q81, Q82, Q83]), "radius" : 0.25 * mm, "tangentPropagation" : true, "allowEdgeOverflow" : false});
        }
        {
            var Q0;
            Q0=makeQuery(id+"F7.opExtrude","CAP_FACE",FACE,{"disambiguationData":[OSD([sQuery(id+"F6.wireOp",EDGE,"E9"),sQuery(id+"F6.wireOp",EDGE,"E10")])],"isStart":false});
            var sketch = newSketch(context, id + "F9", { "sketchPlane" : qUnion([Q0])});
            skCircle(sketch, "E12", {"center": v(5.33, 0) * mm, "radius": 2.48 * mm});
            skSolve(sketch);
        }
        {
            var Q0;
            Q0=makeQuery(id+"F9.imprint","IMPRINT",FACE,{"disambiguationData":[TD([[makeQuery(id+"F9.imprint","IMPRINT",EDGE,{"derivedFrom":sQuery(id+"F9.wireOp",EDGE,"E12")}),1.0]])]});
            extrude(context, id + "F10", {"entities" : qUnion([Q0]), "operationType" : NewBodyOperationType.ADD, "depth" : 2.92 * mm});
        }
    });
